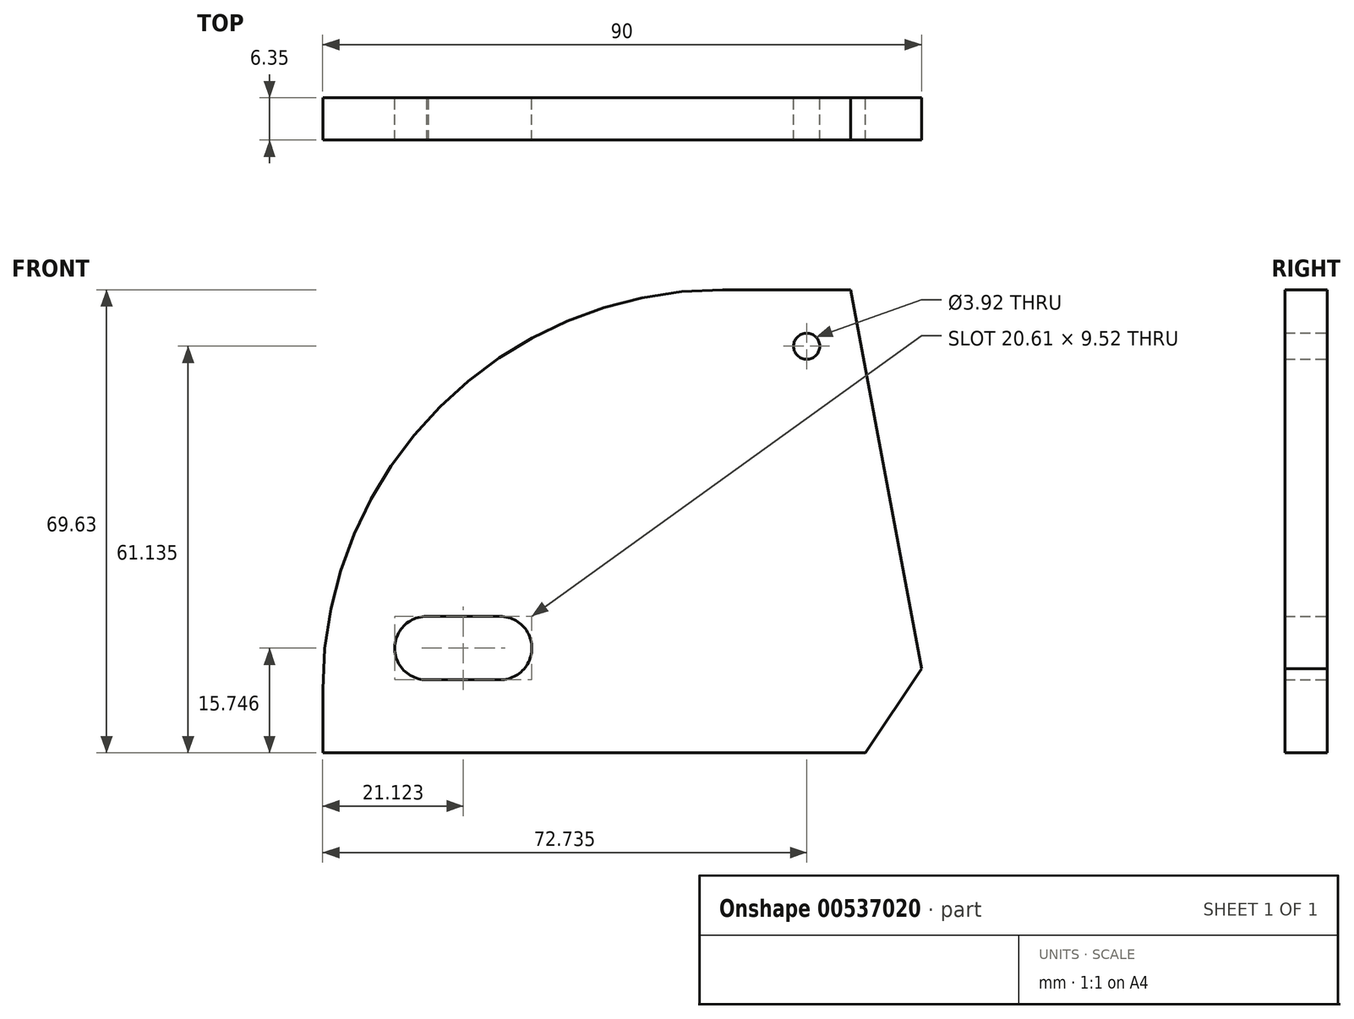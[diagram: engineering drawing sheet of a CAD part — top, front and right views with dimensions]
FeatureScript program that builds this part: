
annotation { "Feature Type Name" : "Feature", "Feature Type Description" : "" }
export const myFeature = defineFeature(function(context is Context, id is Id, definition is map)
    precondition{}
    {
        {
            var Q0;
            Q0=qCreatedBy(makeId("Front.planeOp"),FACE);
            var sketch = newSketch(context, id + "F0", { "sketchPlane" : qUnion([Q0])});
            skLineSegment(sketch, "E0", {"start": v(-70.4, -13.72) * mm, "end": v(-76.54, -84.58) * mm, "construction": true});
            skCircle(sketch, "E1", {"center": v(-70.4, -13.72) * mm, "radius": 1.96 * mm});
            skLineSegment(sketch, "E2", {"start": v(-63.78, -5.23) * mm, "end": v(-53.13, -62.22) * mm});
            skLineSegment(sketch, "E3", {"start": v(-53.13, -62.22) * mm, "end": v(-61.54, -74.86) * mm});
            skLineSegment(sketch, "E4", {"start": v(-61.54, -74.86) * mm, "end": v(-143.13, -74.86) * mm});
            skLineSegment(sketch, "E5", {"start": v(-63.78, -5.23) * mm, "end": v(-83.03, -5.23) * mm});
            skLineSegment(sketch, "E6", {"start": v(-143.13, -74.86) * mm, "end": v(-143.13, -65.34) * mm});
            skArc(sketch, "E7", {"start": v(-83.03, -5.23) * mm, "mid": v(-125.53, -22.84) * mm, "end": v(-143.13, -65.34) * mm});
            skArc(sketch, "E8", {"start": v(-127.21, -54.36) * mm, "mid": v(-132.31, -58.97) * mm, "end": v(-127.5, -63.88) * mm});
            skArc(sketch, "E9", {"start": v(-116.47, -63.88) * mm, "mid": v(-111.7, -59.11) * mm, "end": v(-116.47, -54.35) * mm});
            skLineSegment(sketch, "E10", {"start": v(-127.55, -59.11) * mm, "end": v(-116.47, -59.11) * mm, "construction": true});
            skLineSegment(sketch, "E11", {"start": v(-127.21, -54.36) * mm, "end": v(-116.47, -54.35) * mm});
            skLineSegment(sketch, "E12", {"start": v(-127.5, -63.88) * mm, "end": v(-116.47, -63.88) * mm});
            skSolve(sketch);
        }
        {
            var Q0;
            Q0=qSketchRegion(id+"F0",true);
            extrude(context, id + "F1", {"entities" : qUnion([Q0]), "depth" : 6.35 * mm, "offsetDistance" : 25.4 * mm});
        }
    });
